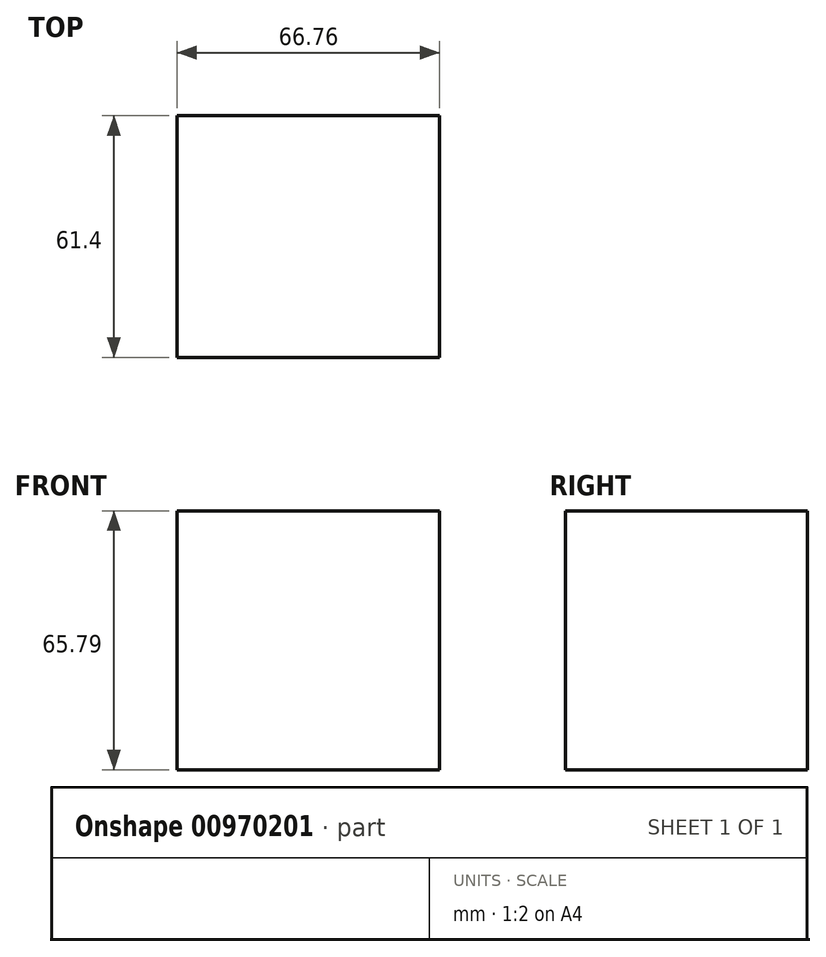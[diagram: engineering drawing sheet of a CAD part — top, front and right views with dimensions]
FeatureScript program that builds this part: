
annotation { "Feature Type Name" : "Feature", "Feature Type Description" : "" }
export const myFeature = defineFeature(function(context is Context, id is Id, definition is map)
    precondition{}
    {
        {
            var Q0;
            Q0=qCreatedBy(makeId("Top.planeOp"),FACE);
            var sketch = newSketch(context, id + "F0", { "sketchPlane" : qUnion([Q0])});
            skLineSegment(sketch, "E0.bottom", {"start": v(-33.23, 30.31) * mm, "end": v(33.53, 30.31) * mm});
            skLineSegment(sketch, "E0.top", {"start": v(-33.23, -31.1) * mm, "end": v(33.53, -31.1) * mm});
            skLineSegment(sketch, "E0.left", {"start": v(-33.23, 30.31) * mm, "end": v(-33.23, -31.1) * mm});
            skLineSegment(sketch, "E0.right", {"start": v(33.53, 30.31) * mm, "end": v(33.53, -31.1) * mm});
            skSolve(sketch);
        }
        {
            var Q0;
            Q0 = qSketchRegion(id + "F0", true);
            extrude(context, id + "F1", {"entities" : qUnion([Q0]), "depth" : 65.8 * mm, "offsetDistance" : 25.4 * mm});
        }
    });
